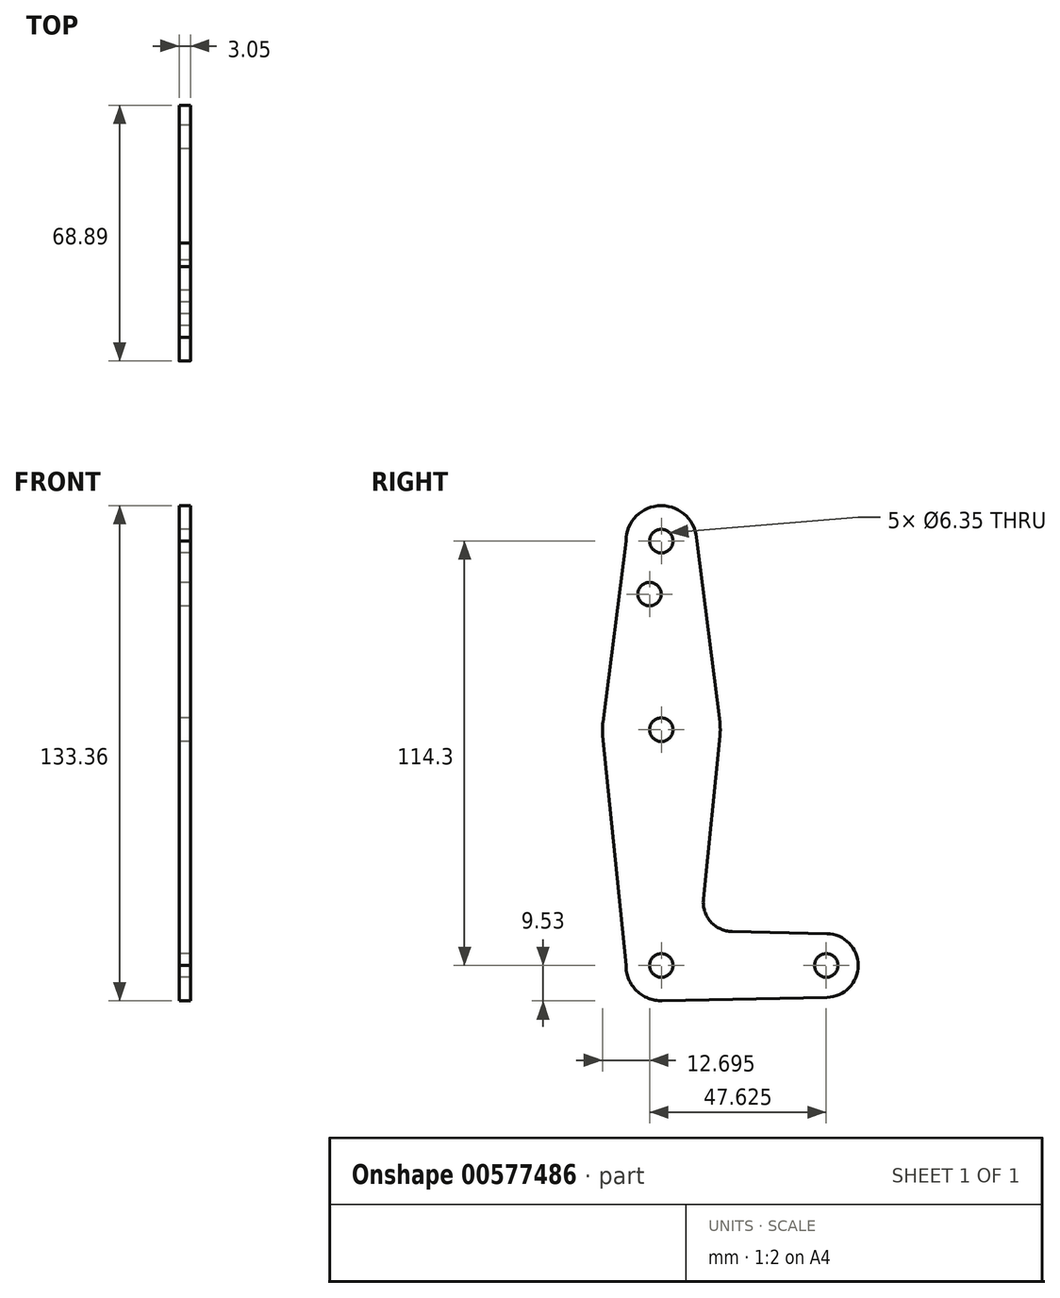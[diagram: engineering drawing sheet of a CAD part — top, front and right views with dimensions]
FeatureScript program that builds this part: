
annotation { "Feature Type Name" : "Feature", "Feature Type Description" : "" }
export const myFeature = defineFeature(function(context is Context, id is Id, definition is map)
    precondition{}
    {
        {
            var Q0;
            Q0=qCreatedBy(makeId("Right.planeOp"),FACE);
            var sketch = newSketch(context, id + "F0", { "sketchPlane" : qUnion([Q0])});
            skLineSegment(sketch, "E0", {"start": v(0, 0) * mm, "end": v(0, 114.3) * mm, "construction": true});
            skCircle(sketch, "E1", {"center": v(0, 114.3) * mm, "radius": 9.53 * mm});
            skCircle(sketch, "E2", {"center": v(0, 63.5) * mm, "radius": 15.88 * mm});
            skCircle(sketch, "E3", {"center": v(0, 0) * mm, "radius": 9.53 * mm});
            skLineSegment(sketch, "E4", {"start": v(0, 0) * mm, "end": v(44.45, 0) * mm, "construction": true});
            skCircle(sketch, "E5", {"center": v(44.45, 0) * mm, "radius": 8.57 * mm});
            skLineSegment(sketch, "E6", {"start": v(9.52, 114.3) * mm, "end": v(15.75, 65.5) * mm});
            skLineSegment(sketch, "E7", {"start": v(-9.52, 114.3) * mm, "end": v(-15.75, 65.5) * mm});
            skLineSegment(sketch, "E8", {"start": v(11.33, 17.87) * mm, "end": v(15.8, 61.9) * mm});
            skLineSegment(sketch, "E9", {"start": v(-9.52, 0) * mm, "end": v(-15.8, 61.9) * mm});
            skLineSegment(sketch, "E10", {"start": v(44.63, 8.57) * mm, "end": v(19.07, 9.12) * mm});
            skLineSegment(sketch, "E11", {"start": v(44.63, -8.57) * mm, "end": v(0, -9.53) * mm});
            skCircle(sketch, "E12", {"center": v(-3.18, 100.03) * mm, "radius": 3.18 * mm});
            skCircle(sketch, "E13", {"center": v(0, 114.3) * mm, "radius": 3.18 * mm});
            skCircle(sketch, "E14", {"center": v(0, 63.5) * mm, "radius": 3.18 * mm});
            skCircle(sketch, "E15", {"center": v(0, 0) * mm, "radius": 3.18 * mm});
            skCircle(sketch, "E16", {"center": v(44.45, 0) * mm, "radius": 3.18 * mm});
            skArc(sketch, "E17.filletArc", {"start": v(11.33, 17.87) * mm, "mid": v(13.29, 11.8) * mm, "end": v(19.07, 9.12) * mm});
            skSolve(sketch);
        }
        {
            var Q0;
            Q0 = qSketchRegion(id + "F0", true);
            extrude(context, id + "F1", {"entities" : qUnion([Q0]), "depth" : 3.05 * mm, "offsetDistance" : 25.4 * mm});
        }
    });
